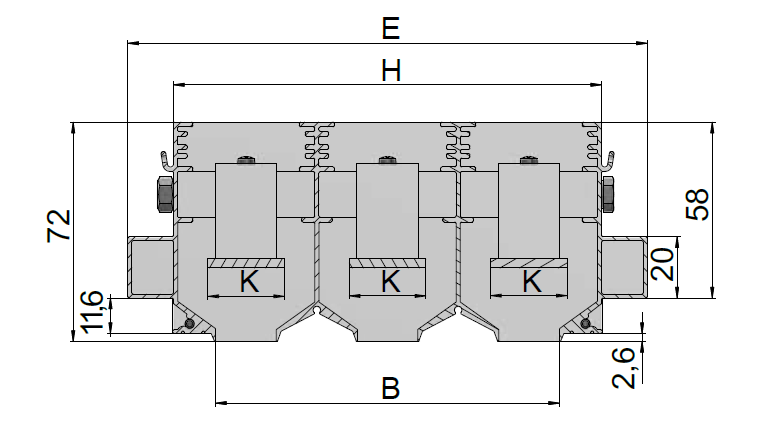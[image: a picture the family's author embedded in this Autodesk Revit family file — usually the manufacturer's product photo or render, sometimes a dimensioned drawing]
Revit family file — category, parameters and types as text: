
# Revit family: GR_Адаптер линейный_Муфта(1)_АДЛ-КСД_R21
name_source: partatom
category: Соединительные детали воздуховодов
units: mm (PartAtom-declared; Revit-internal decimal feet)

## family parameters
Всегда вертикально = Да
Заголовок OmniClass = Metal Ducts
На основе рабочей плоскости = Нет
Номер OmniClass = 23.75.70.14.31
Общий = Нет
При загрузке вырезать с полостями = Нет
Размер круглого соединителя = Использовать диаметр
Тип детали = Мультипорт

## types (6) — shared parameters
ADSK_URL страницы изделия = https://grilles.ru
ADSK_Версия Revit = 2021
ADSK_Единица измерения = шт.
ADSK_Завод-изготовитель = ООО "ВЕНТРЕШЕТКИКОМ"
ADSK_Код изделия = 002010
ADSK_Количество = 1
ADSK_Материал = ADSK_Оцинкованная сталь
ADSK_Наименование = АДЛ-КСД, адаптер вентиляционной решётки
Изготовитель = ООО "ВЕНТРЕШЕТКИКОМ"
Корпус_Металл_Толщина = 1 мм
Муфта_Металл_Толщина = 1 мм
zero-valued in all types: Отметка по умолчанию

## per-type parameters (varying)
| type | Корпус_Высота | Корпус_Длина | Решётка_Высота | Решётка_Положение_Центр |
| АДЛ-КСД 1-20 | 182 мм | 90 мм | 48 мм | 45 мм |
| АДЛ-КСД 2-20 | 222 мм | 128 мм | 86 мм | 64 мм |
| АДЛ-КСД 3-20 | 222 мм | 166 мм | 124 мм | 83 мм |
| АДЛ-КСД 4-20 | 272 мм | 204 мм | 162 мм | 102 мм |
| АДЛ-КСД 5-20 | 272 мм | 242 мм | 200 мм | 121 мм |
| АДЛ-КСД 6-20 | 337 мм | 280 мм | 238 мм | 140 мм |

note: column(s) folded — value = type name in every type: ADSK_Марка
